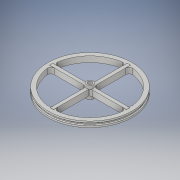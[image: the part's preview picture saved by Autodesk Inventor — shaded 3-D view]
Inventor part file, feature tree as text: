
AUTODESK INVENTOR PART (.ipt)
format: ipt  version: 2018 (Build 220112000, 112)  size: 447,488 bytes
history: native  units: in
note: dims shown in document units (in); Inventor stores cm internally (conversion verified against a paired STEP export)
features: sketch x10, extrude x9, fillet x5
ambient origin geometry x8: Origin, YZ Plane, XZ Plane, XY Plane, X Axis, Y Axis, Z Axis, Center Point
bodies: Solid1 (feature_tree)
feature tree (24):
  extrude  "Extrusion1"  Depth=0.0938in TaperAngle=0.0deg
  sketch  "Sketch2"  dims[d3=3.188in d4=0.0625in d5=0.0in]
  sketch  "Sketch3"  dims[d6=3.188in d7=0.0625in d8=0.0in d9=0.03in]
  extrude  "Extrusion2"  Depth=0.0625in TaperAngle=0.0deg
  extrude  "Extrusion3"  Depth=0.0625in TaperAngle=0.0deg
  fillet  "Fillet1"  Radius=0.03in
  extrude  "Extrusion4"  Depth=0.25in TaperAngle=0.0deg
  extrude  "Extrusion5"  Depth=0.225in TaperAngle=0.0deg
  extrude  "Extrusion6"  Depth=0.225in TaperAngle=0.0deg
  fillet  "Fillet2"  Radius=0.125in
  fillet  "Fillet3"  Radius=0.125in
  fillet  "Fillet4"  Radius=0.125in
  extrude  "Extrusion7"  Depth=0.225in TaperAngle=0.0deg
  extrude  "Extrusion8"  Depth=0.225in TaperAngle=0.0deg
  extrude  "Extrusion9"  Depth=0.125in
  fillet  "Fillet5"  [1 undecoded]
  sketch  "Sketch1"  dims[d0=3.125in d1=0.0938in d2=0.0in]
  sketch  "Sketch4"  dims[d10=2.875in d11=0.25in d12=0.0in]
  sketch  "Sketch5"  dims[d13=0.125in d14=0.225in d15=0.0in]
  sketch  "Sketch6"  dims[d16=0.125in d17=0.225in d18=0.0in d19=0.125in d20=0.125in d21=0.125in]
  sketch  "Sketch7"  dims[d22=0.25in d23=0.225in d24=0.0in]
  sketch  "Sketch8"  dims[d25=0.157in d26=0.225in d27=0.0in]
  sketch  "Sketch9"  dims[d28=0.125in d29=0.35in d30=0.0in d31=0.0in d32=0.125in]
  sketch  "Sketch10"
note: 1 required parameter value undecoded (feature->parameter linkage not recoverable at this tier; creation-order binding heuristic only, values carry confidence <= 0.55)
